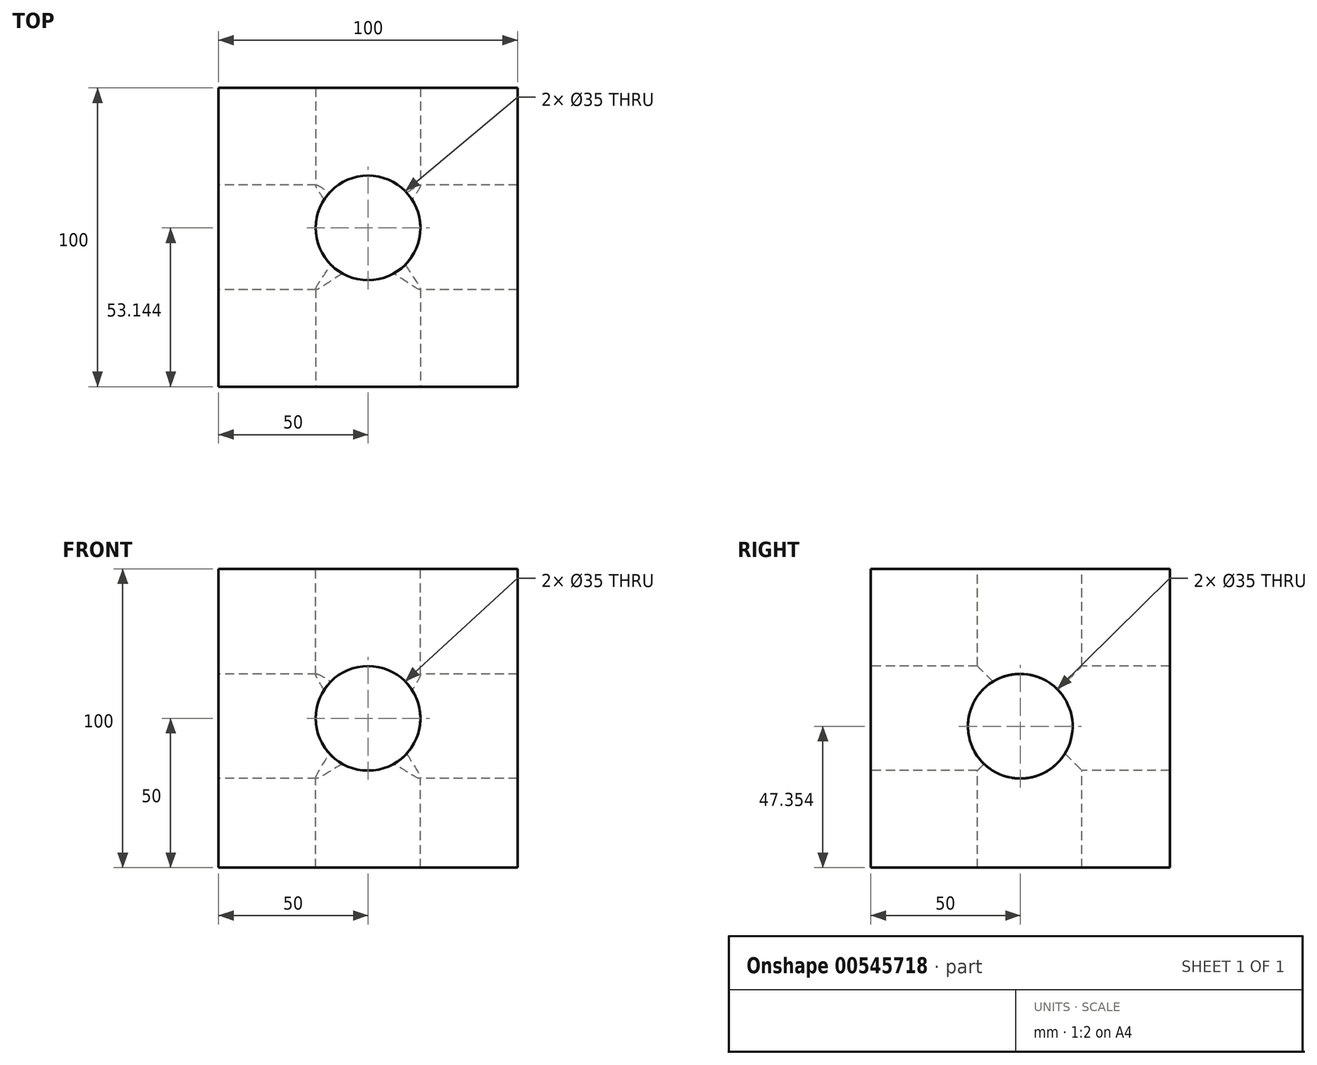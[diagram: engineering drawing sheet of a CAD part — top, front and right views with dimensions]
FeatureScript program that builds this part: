
annotation { "Feature Type Name" : "Feature", "Feature Type Description" : "" }
export const myFeature = defineFeature(function(context is Context, id is Id, definition is map)
    precondition{}
    {
        {
            var Q0;
            Q0=qCreatedBy(makeId("Front.planeOp"),FACE);
            var sketch = newSketch(context, id + "F0", { "sketchPlane" : qUnion([Q0])});
            skLineSegment(sketch, "E0.bottom", {"start": v(-50, 50) * mm, "end": v(50, 50) * mm});
            skLineSegment(sketch, "E0.top", {"start": v(-50, -50) * mm, "end": v(50, -50) * mm});
            skLineSegment(sketch, "E0.left", {"start": v(-50, 50) * mm, "end": v(-50, -50) * mm});
            skLineSegment(sketch, "E0.right", {"start": v(50, 50) * mm, "end": v(50, -50) * mm});
            skPoint(sketch, "E0.middle", {"position": v(0, 0) * mm});
            skSolve(sketch);
        }
        {
            var Q0;
            Q0 = qSketchRegion(id + "F0", true);
            extrude(context, id + "F1", {"entities" : qUnion([Q0]), "depth" : 100 * mm, "offsetDistance" : 25 * mm, "symmetric" : true});
        }
        {
            var Q0;
            Q0=makeQuery(id+"F1.opExtrude","CAP_FACE",FACE,{"disambiguationData":[OSD([sQuery(id+"F0.wireOp",EDGE,"E0.bottom"),sQuery(id+"F0.wireOp",EDGE,"E0.top"),sQuery(id+"F0.wireOp",EDGE,"E0.left"),sQuery(id+"F0.wireOp",EDGE,"E0.right")])],"isStart":false});
            var sketch = newSketch(context, id + "F2", { "sketchPlane" : qUnion([Q0])});
            skCircle(sketch, "E1", {"center": v(0, 0) * mm, "radius": 17.5 * mm});
            skSolve(sketch);
        }
        {
            var Q0;
            Q0 = qSketchRegion(id + "F2", true);
            extrude(context, id + "F3", {"entities" : qUnion([Q0]), "operationType" : NewBodyOperationType.REMOVE, "endBound" : BoundingType.UP_TO_NEXT, "oppositeDirection" : true, "depth" : 25 * mm, "offsetDistance" : 25 * mm});
        }
        {
            var Q0;
            Q0=makeQuery(id+"F1.opExtrude","SWEPT_FACE",FACE,{"disambiguationData":[OSD([sQuery(id+"F0.wireOp",EDGE,"E0.left")])]});
            var sketch = newSketch(context, id + "F4", { "sketchPlane" : qUnion([Q0])});
            skCircle(sketch, "E2", {"center": v(0, -2.65) * mm, "radius": 17.5 * mm});
            skSolve(sketch);
        }
        {
            var Q0;
            Q0=makeQuery(id+"F4.imprint","IMPRINT",FACE,{"disambiguationData":[TD([[makeQuery(id+"F4.imprint","IMPRINT",EDGE,{"derivedFrom":sQuery(id+"F4.wireOp",EDGE,"E2")}),1.0]])]});
            var Q1;
            Q1=makeQuery(id+"F1.opExtrude","SWEPT_FACE",FACE,{"disambiguationData":[OSD([sQuery(id+"F0.wireOp",EDGE,"E0.right")])]});
            extrude(context, id + "F5", {"entities" : qUnion([Q0]), "operationType" : NewBodyOperationType.REMOVE, "endBound" : BoundingType.UP_TO_SURFACE, "oppositeDirection" : true, "depth" : 25 * mm, "endBoundEntityFace" : qUnion([Q1]), "offsetDistance" : 25 * mm});
        }
        {
            var Q0;
            Q0=makeQuery(id+"F1.opExtrude","SWEPT_FACE",FACE,{"disambiguationData":[OSD([sQuery(id+"F0.wireOp",EDGE,"E0.bottom")])]});
            var sketch = newSketch(context, id + "F6", { "sketchPlane" : qUnion([Q0])});
            skCircle(sketch, "E3", {"center": v(0, 3.14) * mm, "radius": 17.5 * mm});
            skSolve(sketch);
        }
        {
            var Q0;
            Q0 = qSketchRegion(id + "F6", true);
            var Q1;
            Q1=makeQuery(id+"F1.opExtrude","SWEPT_FACE",FACE,{"disambiguationData":[OSD([sQuery(id+"F0.wireOp",EDGE,"E0.top")])]});
            extrude(context, id + "F7", {"entities" : qUnion([Q0]), "operationType" : NewBodyOperationType.REMOVE, "endBound" : BoundingType.UP_TO_SURFACE, "oppositeDirection" : true, "depth" : 25 * mm, "endBoundEntityFace" : qUnion([Q1]), "offsetDistance" : 25 * mm});
        }
    });
